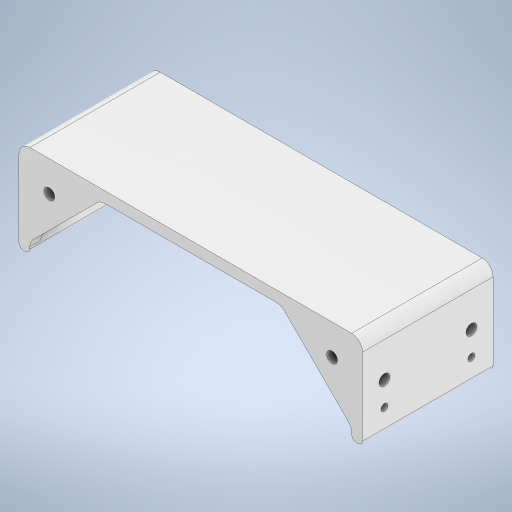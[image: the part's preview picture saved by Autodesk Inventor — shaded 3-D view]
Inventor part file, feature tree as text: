
AUTODESK INVENTOR PART (.ipt)
format: ipt  version: 2024.3 (Build 283343000, 343)  size: 409,088 bytes
history: native  units: mm
features: sketch x8, extrude x7, fillet x3, other x1, hole x1, projected_geometry x1
ambient origin geometry x8: Origin, YZ Plane, XZ Plane, XY Plane, X Axis, Y Axis, Z Axis, Center Point
bodies: Body1 (feature_tree)
feature tree (21):
  other  "ソリッド1"
  extrude  "押し出し1"  Depth=158.0mm
  extrude  "押し出し3"  Depth=250.0mm
  extrude  "押し出し4"  Depth=5.0mm
  hole  "穴2"  [1 undecoded]
  extrude  "押し出し5"  Depth=50.0mm
  extrude  "押し出し6"  Depth=50.0mm
  extrude  "押し出し7"  Depth=30.0mm
  fillet  "フィレット4"  Radius=5.0mm
  fillet  "フィレット6"  Radius=50.0mm
  extrude  "押し出し8"  Depth=50.0mm
  fillet  "フィレット7"  Radius=30.0mm
  sketch  "スケッチ1"
  sketch  "スケッチ5"
  sketch  "スケッチ6"
  sketch  "スケッチ7"
  sketch  "スケッチ8"
  sketch  "スケッチ9"
  sketch  "スケッチ10"
  sketch  "スケッチ12"
  projected_geometry  "投影ループ1"
note: 1 required parameter value undecoded (feature->parameter linkage not recoverable at this tier; creation-order binding heuristic only, values carry confidence <= 0.55)
